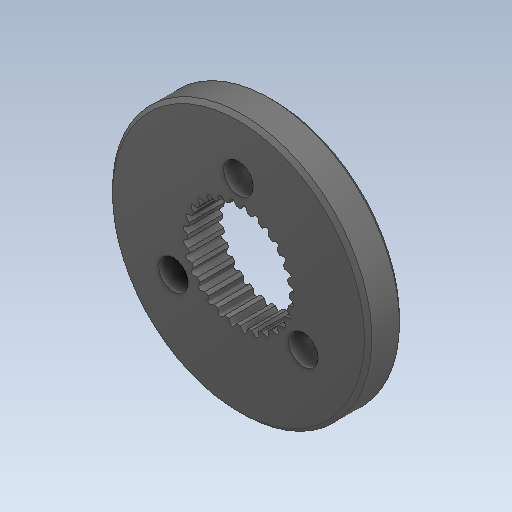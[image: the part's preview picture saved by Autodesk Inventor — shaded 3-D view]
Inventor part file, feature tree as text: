
AUTODESK INVENTOR PART (.ipt)
format: ipt  version: 2020 (Build 240168000, 168)  size: 279,040 bytes
history: native  units: in
note: dims shown in document units (in); Inventor stores cm internally (conversion verified against a paired STEP export)
features: chamfer x1
ambient origin geometry x8: Origin, YZ Plane, XZ Plane, XY Plane, X Axis, Y Axis, Z Axis, Center Point
bodies: Solid1 (feature_tree)
feature tree (1):
  chamfer  "Chamfer1"  [1 undecoded]
note: 1 required parameter value undecoded (feature->parameter linkage not recoverable at this tier; creation-order binding heuristic only, values carry confidence <= 0.55)
